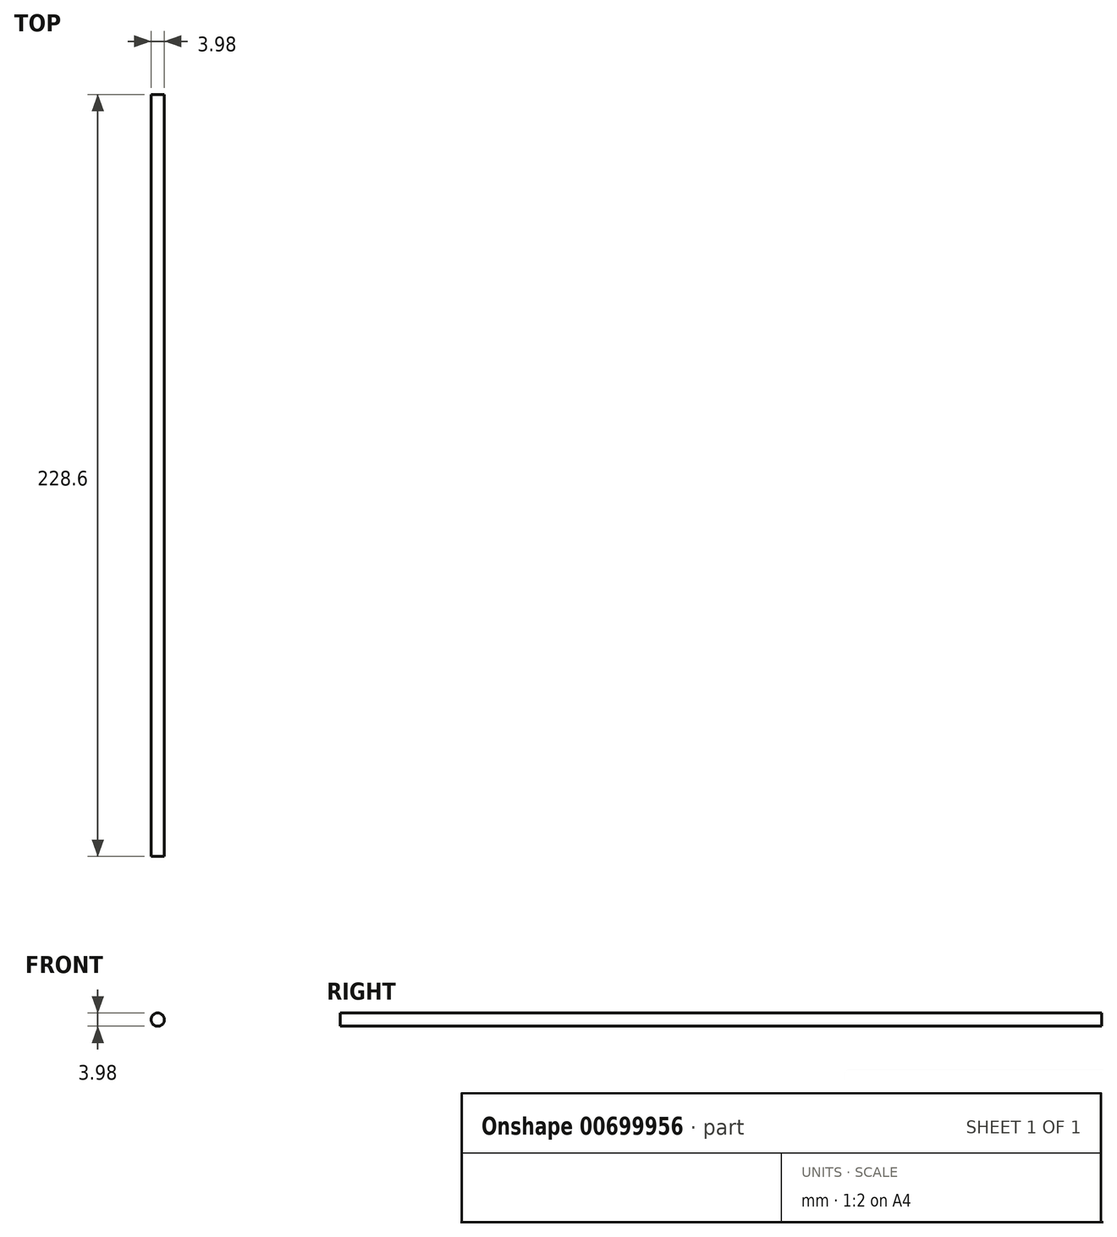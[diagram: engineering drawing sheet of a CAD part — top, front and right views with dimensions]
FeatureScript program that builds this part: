
annotation { "Feature Type Name" : "Feature", "Feature Type Description" : "" }
export const myFeature = defineFeature(function(context is Context, id is Id, definition is map)
    precondition{}
    {
        {
            var Q0;
            Q0=qCreatedBy(makeId("Front.planeOp"),FACE);
            var sketch = newSketch(context, id + "F0", { "sketchPlane" : qUnion([Q0])});
            skCircle(sketch, "E0", {"center": v(0, 0) * mm, "radius": 2 * mm});
            skSolve(sketch);
        }
        {
            var Q0;
            Q0=makeQuery(id+"F0.imprint","IMPRINT",FACE,{"disambiguationData":[TD([[makeQuery(id+"F0.imprint","IMPRINT",EDGE,{"derivedFrom":sQuery(id+"F0.wireOp",EDGE,"E0")}),1.0]])]});
            extrude(context, id + "F1", {"entities" : qUnion([Q0]), "depth" : 228.6 * mm, "offsetDistance" : 25.4 * mm});
        }
    });
